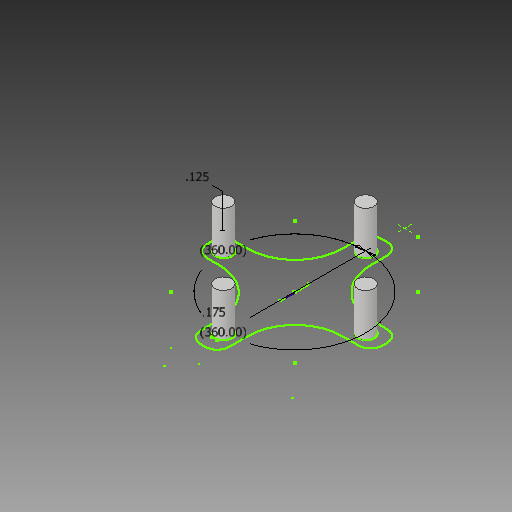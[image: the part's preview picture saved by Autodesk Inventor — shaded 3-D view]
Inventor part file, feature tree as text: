
AUTODESK INVENTOR PART (.ipt)
format: ipt  version: 2019 (Build 230136000, 136)  size: 147,968 bytes
history: native  units: in
note: dims shown in document units (in); Inventor stores cm internally (conversion verified against a paired STEP export)
features: extrude x4, sketch x2, plane x1
ambient origin geometry x8: Origin, YZ Plane, XZ Plane, XY Plane, X Axis, Y Axis, Z Axis, Center Point
bodies: Body1 (feature_tree)
feature tree (7):
  sketch  "Sketch1"  dims[d1=1.5748in d3=360.0deg d5=0.175in]
  extrude  "Extrusion4"  Depth=0.175in
  plane  "Work Plane2"
  extrude  "Extrusion5"  Depth=0.45in
  extrude  "Extrusion6"  Depth=0.45in
  extrude  "Extrusion7"  Depth=0.45in TaperAngle=0.0deg
  sketch  "Sketch2"  dims[d6=1.5748in d8=360.0deg d10=0.15in d11=0.15in d21=0.2in d24=0.45in d25=0.0in d26=0.225in d27=0.45in d28=0.0in d29=0.125in d30=0.2in d31=0.0in d32=0.2in d33=0.0in]
